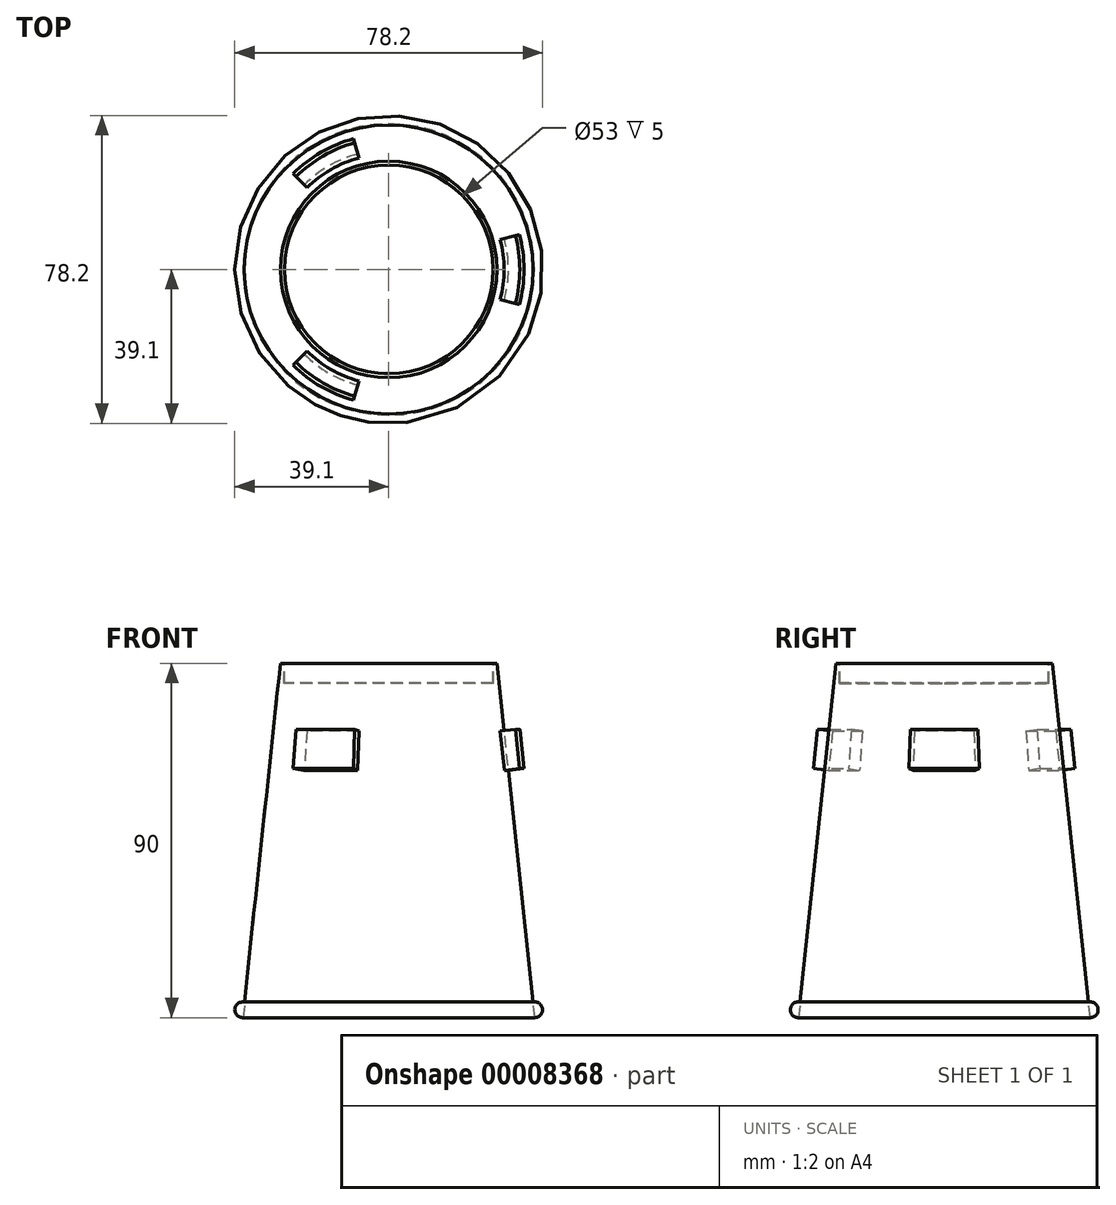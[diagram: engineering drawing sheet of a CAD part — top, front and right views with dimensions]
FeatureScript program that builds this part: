
annotation { "Feature Type Name" : "Feature", "Feature Type Description" : "" }
export const myFeature = defineFeature(function(context is Context, id is Id, definition is map)
    precondition{}
    {
        {
            var Q0;
            Q0=qCreatedBy(makeId("Front.planeOp"),FACE);
            var sketch = newSketch(context, id + "F0", { "sketchPlane" : qUnion([Q0])});
            skLineSegment(sketch, "E0", {"start": v(0, 0) * mm, "end": v(0, 90) * mm});
            skLineSegment(sketch, "E1", {"start": v(0, 90) * mm, "end": v(27.5, 90) * mm});
            skLineSegment(sketch, "E2", {"start": v(27.5, 90) * mm, "end": v(37.1, 0) * mm});
            skLineSegment(sketch, "E3", {"start": v(37.1, 0) * mm, "end": v(0, 0) * mm});
            skSolve(sketch);
        }
        {
            var Q0;
            Q0=makeQuery(id+"F0.imprint","IMPRINT",FACE,{"disambiguationData":[TD([[makeQuery(id+"F0.imprint","IMPRINT",EDGE,{"derivedFrom":sQuery(id+"F0.wireOp",EDGE,"E0")}),-1.0]])]});
            var Q1;
            Q1=sQuery(id+"F0.wireOp",EDGE,"E0");
            revolve(context, id + "F1", {"entities" : qUnion([Q0]), "axis" : qUnion([Q1]), "revolveType" : RevolveType.FULL});
        }
        {
            var Q0;
            Q0=makeQuery(id+"F1.opRevolve","SWEPT_FACE",FACE,{"disambiguationData":[OSD([sQuery(id+"F0.wireOp",EDGE,"E1")])]});
            var sketch = newSketch(context, id + "F2", { "sketchPlane" : qUnion([Q0])});
            skCircle(sketch, "E4", {"center": v(0, 0) * mm, "radius": 26.5 * mm});
            skSolve(sketch);
        }
        {
            var Q0;
            Q0=makeQuery(id+"F2.imprint","IMPRINT",FACE,{"disambiguationData":[TD([[makeQuery(id+"F2.imprint","IMPRINT",EDGE,{"derivedFrom":sQuery(id+"F2.wireOp",EDGE,"E4")}),1.0]])]});
            extrude(context, id + "F3", {"entities" : qUnion([Q0]), "operationType" : NewBodyOperationType.REMOVE, "oppositeDirection" : true, "depth" : 5 * mm});
        }
        {
            var Q0;
            Q0=makeQuery(id+"F1.opRevolve","SWEPT_FACE",FACE,{"disambiguationData":[OSD([sQuery(id+"F0.wireOp",EDGE,"E3")])]});
            shell(context, id + "F4", {"entities" : qUnion([Q0]), "thickness" : 0.1 * mm});
        }
        {
            var Q0;
            Q0=qCreatedBy(makeId("Front.planeOp"),FACE);
            var sketch = newSketch(context, id + "F5", { "sketchPlane" : qUnion([Q0])});
            skLineSegment(sketch, "E5", {"start": v(37.1, 0) * mm, "end": v(37.1, 2) * mm});
            skArc(sketch, "E6", {"start": v(37.1, 0) * mm, "mid": v(39.09, 2.23) * mm, "end": v(36.65, 3.95) * mm});
            skPoint(sketch, "E7", {"position": v(36.65, 3.95) * mm});
            skLineSegment(sketch, "E8", {"start": v(36.65, 3.95) * mm, "end": v(37.1, 0) * mm});
            skSolve(sketch);
        }
        {
            var Q0;
            Q0 = qSketchRegion(id + "F5", true);
            var Q1;
            Q1=sQuery(id+"F0.wireOp",EDGE,"E0");
            revolve(context, id + "F6", {"operationType" : NewBodyOperationType.ADD, "entities" : qUnion([Q0]), "axis" : qUnion([Q1]), "revolveType" : RevolveType.FULL});
        }
        {
            var Q0;
            Q0=qCreatedBy(makeId("Front.planeOp"),FACE);
            var sketch = newSketch(context, id + "F7", { "sketchPlane" : qUnion([Q0])});
            skLineSegment(sketch, "E9", {"start": v(29.33, 72.81) * mm, "end": v(33.31, 73.24) * mm});
            skLineSegment(sketch, "E10", {"start": v(33.31, 73.24) * mm, "end": v(34.37, 63.3) * mm});
            skLineSegment(sketch, "E11", {"start": v(34.37, 63.3) * mm, "end": v(30.4, 62.87) * mm});
            skLineSegment(sketch, "E12", {"start": v(29.33, 72.81) * mm, "end": v(30.4, 62.87) * mm});
            skSolve(sketch);
        }
        {
            var Q0;
            Q0 = qSketchRegion(id + "F7", true);
            var Q1;
            Q1=sQuery(id+"F0.wireOp",EDGE,"E0");
            revolve(context, id + "F8", {"operationType" : NewBodyOperationType.ADD, "entities" : qUnion([Q0]), "axis" : qUnion([Q1]), "revolveType" : RevolveType.TWO_DIRECTIONS, "angle" : 135 * degree, "angleBack" : 225 * degree});
        }
        {
            var Q0;
            Q0 = qSketchRegion(id + "F7", true);
            var Q1;
            Q1=sQuery(id+"F0.wireOp",EDGE,"E0");
            revolve(context, id + "F9", {"operationType" : NewBodyOperationType.REMOVE, "entities" : qUnion([Q0]), "axis" : qUnion([Q1]), "revolveType" : RevolveType.TWO_DIRECTIONS, "oppositeDirection" : true, "angle" : 105 * degree, "angleBack" : 255 * degree});
        }
        {
            var Q0;
            Q0 = qSketchRegion(id + "F7", true);
            var Q1;
            Q1=sQuery(id+"F0.wireOp",EDGE,"E0");
            revolve(context, id + "F10", {"operationType" : NewBodyOperationType.ADD, "entities" : qUnion([Q0]), "axis" : qUnion([Q1]), "revolveType" : RevolveType.TWO_DIRECTIONS, "angle" : 15 * degree, "angleBack" : 345 * degree});
        }
    });
